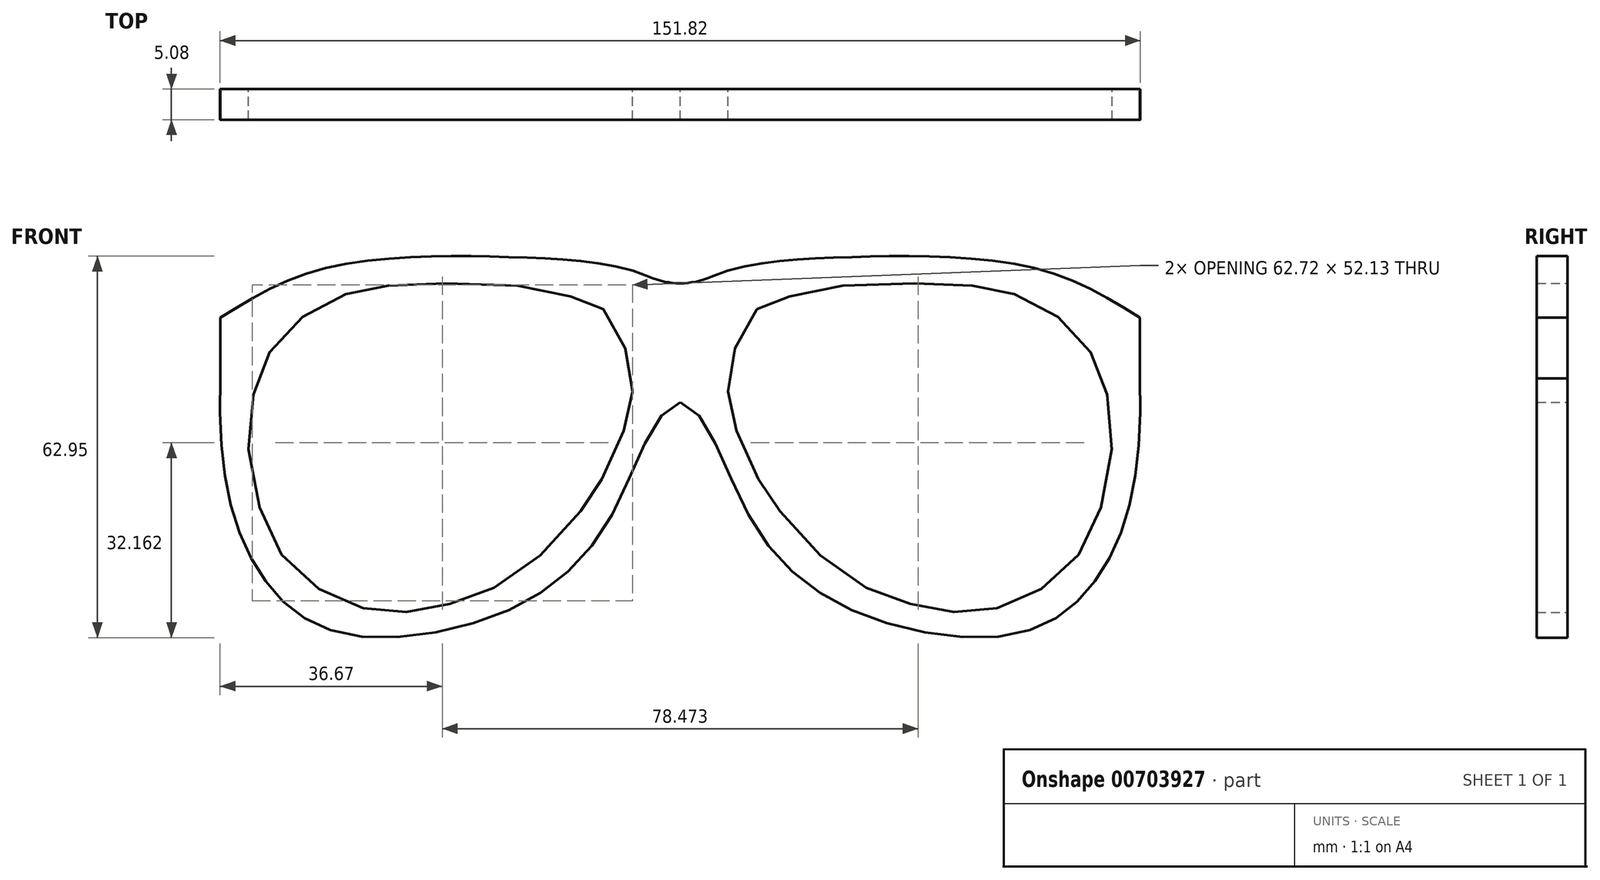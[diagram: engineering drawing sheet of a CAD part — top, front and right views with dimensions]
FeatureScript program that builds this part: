
annotation { "Feature Type Name" : "Feature", "Feature Type Description" : "" }
export const myFeature = defineFeature(function(context is Context, id is Id, definition is map)
    precondition{}
    {
        {
            var Q0;
            Q0=qCreatedBy(makeId("Front.planeOp"),FACE);
            var sketch = newSketch(context, id + "F0", { "sketchPlane" : qUnion([Q0])});
            skFitSpline(sketch, "E0", {"points": [v(0.5, 36.37) * mm, v(1.66, 43.48) * mm, v(5.33, 50.03) * mm, v(9.21, 51.67) * mm, v(18.55, 53.72) * mm, v(36.6, 54.1) * mm, v(44.54, 53.33) * mm, v(51.97, 50.65) * mm, v(59.13, 44.63) * mm, v(62.46, 38.1) * mm, v(63.87, 27.6) * mm, v(61.3, 15.19) * mm, v(56.32, 7) * mm, v(48.25, 1.75) * mm, v(41.05, 0) * mm, v(34, 0.55) * mm, v(26.58, 2.65) * mm, v(17.75, 7.55) * mm, v(8.65, 17.13) * mm, v(5.75, 21.5) * mm, v(1.59, 30.82) * mm, v(0.5, 36.37) * mm]});
            skLineSegment(sketch, "E1", {"start": v(-7.37, 51.98) * mm, "end": v(-7.37, 34.6) * mm});
            skLineSegment(sketch, "E2", {"start": v(68.5, 48.6) * mm, "end": v(68.5, 38.56) * mm});
            skFitSpline(sketch, "E3", {"points": [v(-7.37, 51.98) * mm, v(4.65, 57.31) * mm, v(18.55, 58.5) * mm, v(34.76, 58.63) * mm, v(53.97, 55.94) * mm, v(68.5, 48.6) * mm], "startDerivative": vector(53.92, 51.36) * mm, "endDerivative": vector(68.05, -41.27) * mm});
            skFitSpline(sketch, "E4", {"points": [v(68.5, 38.56) * mm, v(66.95, 18.46) * mm, v(60.56, 4.46) * mm, v(48.08, -3.61) * mm, v(21.65, 0) * mm, v(3.64, 16.53) * mm, v(-7.37, 34.6) * mm], "startDerivative": vector(3.2, -134.34) * mm, "endDerivative": vector(-78.9, 14.24) * mm});
            skSolve(sketch);
        }
        {
            var Q0;
            Q0=makeQuery(id+"F0.imprint","IMPRINT",FACE,{"disambiguationData":[TD([[makeQuery(id+"F0.imprint","IMPRINT",EDGE,{"derivedFrom":sQuery(id+"F0.wireOp",EDGE,"E0")}),1.0]])]});
            extrude(context, id + "F1", {"entities" : qUnion([Q0]), "depth" : 5.08 * mm, "offsetDistance" : 25.4 * mm});
        }
        {
            var Q0;
            Q0=makeQuery(id+"F1.opExtrude","SWEPT_BODY",BODY,{"disambiguationData":[OSD([sQuery(id+"F0.wireOp",EDGE,"E0"),sQuery(id+"F0.wireOp",EDGE,"E1"),sQuery(id+"F0.wireOp",EDGE,"E2"),sQuery(id+"F0.wireOp",EDGE,"E3"),sQuery(id+"F0.wireOp",EDGE,"E4")])]});
            var Q1;
            Q1=makeQuery(id+"F1.opExtrude","SWEPT_FACE",FACE,{"disambiguationData":[OSD([sQuery(id+"F0.wireOp",EDGE,"E1")])]});
            mirror(context, id + "F2", {"operationType" : NewBodyOperationType.ADD, "entities" : qUnion([Q0]), "mirrorPlane" : qUnion([Q1])});
        }
        {
            var Q0;
            {var subQ0=makeQuery(id+"F1.opExtrude","SWEPT_EDGE",EDGE,{"disambiguationData":[OSD([sQuery(id+"F0.wireOp",EDGE,"E1"),sQuery(id+"F0.wireOp",EDGE,"E3")])]});Q0=makeQuery(id+"F2.boolean.opBoolean","MERGE",EDGE,{"derivedFrom":[subQ0,makeQuery(id+"F2.opPattern","COPY",EDGE,{"derivedFrom":subQ0,"instanceName":"1"})]});}
            fillet(context, id + "F3", {"entities" : qUnion([Q0]), "radius" : 12.7 * mm, "tangentPropagation" : true, "allowEdgeOverflow" : false});
        }
    });
